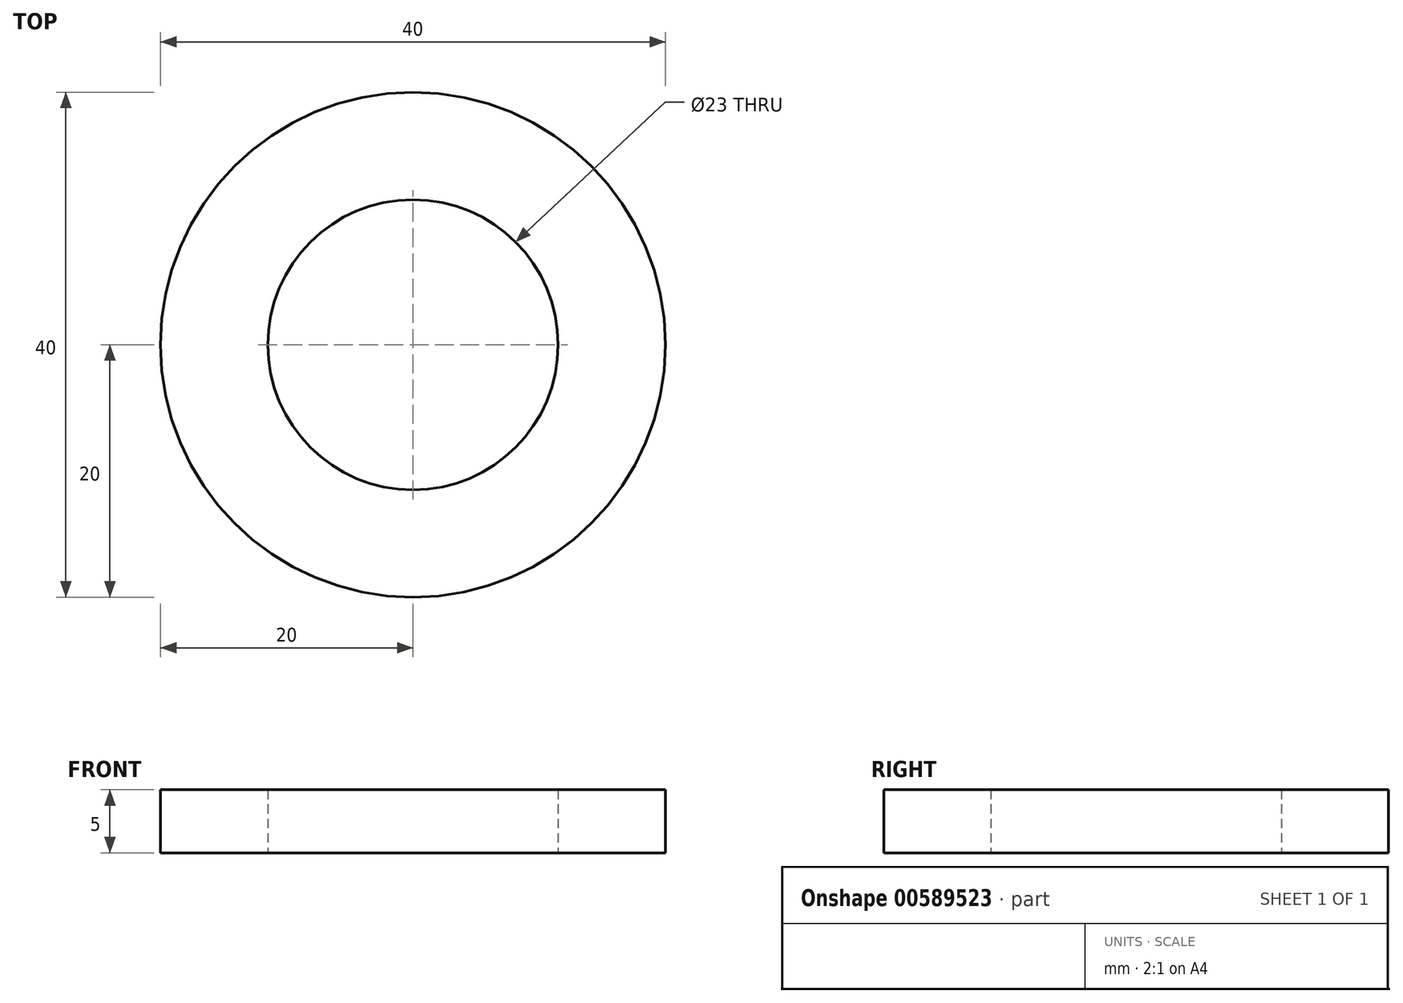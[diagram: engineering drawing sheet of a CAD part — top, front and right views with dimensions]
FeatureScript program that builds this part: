
annotation { "Feature Type Name" : "Feature", "Feature Type Description" : "" }
export const myFeature = defineFeature(function(context is Context, id is Id, definition is map)
    precondition{}
    {
        {
            var Q0;
            Q0=qCreatedBy(makeId("Top.planeOp"),FACE);
            var sketch = newSketch(context, id + "F0", { "sketchPlane" : qUnion([Q0])});
            skCircle(sketch, "E0", {"center": v(0, 0) * mm, "radius": 11.5 * mm});
            skCircle(sketch, "E1", {"center": v(0, 0) * mm, "radius": 20 * mm});
            skSolve(sketch);
        }
        {
            var Q0;
            Q0=makeQuery(id+"F0.imprint","IMPRINT",FACE,{"disambiguationData":[TD([[makeQuery(id+"F0.imprint","IMPRINT",EDGE,{"derivedFrom":sQuery(id+"F0.wireOp",EDGE,"E0")}),-1.0]])]});
            extrude(context, id + "F1", {"entities" : qUnion([Q0]), "depth" : 5 * mm, "offsetDistance" : 25 * mm});
        }
    });
